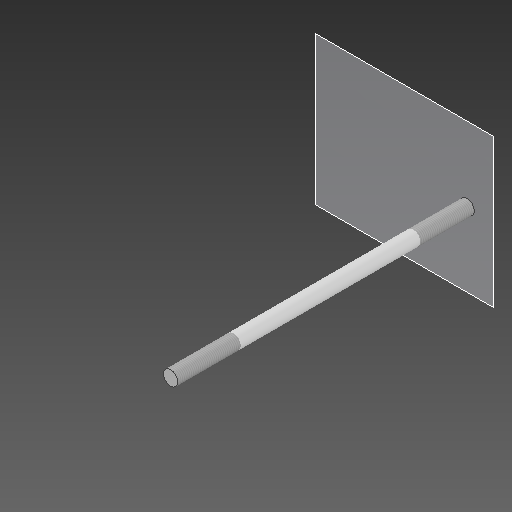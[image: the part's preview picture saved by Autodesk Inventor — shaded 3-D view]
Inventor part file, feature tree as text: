
AUTODESK INVENTOR PART (.ipt)
format: ipt  version: 2021 (Build 250183000, 183)  size: 84,480 bytes
history: native  units: in
note: dims shown in document units (in); Inventor stores cm internally (conversion verified against a paired STEP export)
features: other x3, sketch x1, plane x1
ambient origin geometry x8: Origin, YZ Plane, XZ Plane, XY Plane, X Axis, Y Axis, Z Axis, Center Point
bodies: Solid1 (feature_tree)
feature tree (5):
  other  "Eje roscado base soporte tubo.ipt"
  other  "Solid1::Eje roscado base soporte tubo.ipt"
  other  "TaggingFeature1"
  sketch  "Sketch1"  dims[d0=0.3937in]
  plane  "Work Plane1"
